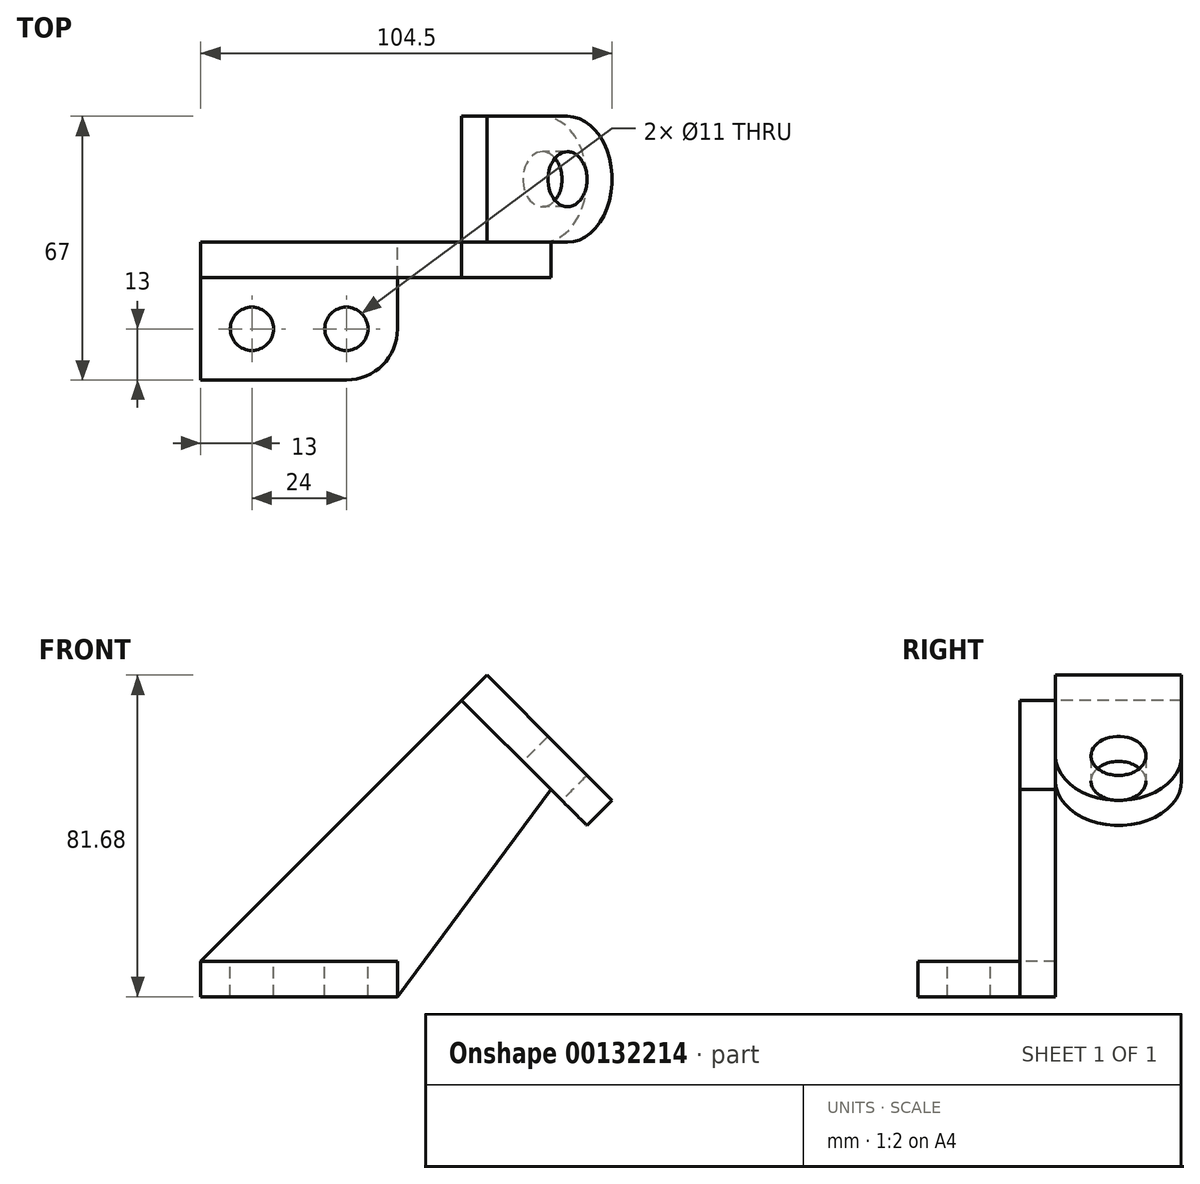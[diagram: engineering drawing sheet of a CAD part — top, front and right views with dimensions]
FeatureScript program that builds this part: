
annotation { "Feature Type Name" : "Feature", "Feature Type Description" : "" }
export const myFeature = defineFeature(function(context is Context, id is Id, definition is map)
    precondition{}
    {
        {
            var Q0;
            Q0=qCreatedBy(makeId("Front.planeOp"),FACE);
            var sketch = newSketch(context, id + "F0", { "sketchPlane" : qUnion([Q0])});
            skLineSegment(sketch, "E0", {"start": v(0, 0) * mm, "end": v(75.31, 75.31) * mm});
            skLineSegment(sketch, "E1", {"start": v(75.31, 75.31) * mm, "end": v(97.94, 52.69) * mm});
            skLineSegment(sketch, "E2", {"start": v(97.94, 52.69) * mm, "end": v(59, 0) * mm});
            skLineSegment(sketch, "E3", {"start": v(59, 0) * mm, "end": v(0, 0) * mm});
            skLineSegment(sketch, "E4", {"start": v(54.11, 66.37) * mm, "end": v(119.02, 66.37) * mm, "construction": true});
            skPoint(sketch, "E5", {"position": v(86.63, 64) * mm});
            skSolve(sketch);
        }
        {
            var Q0;
            Q0 = qSketchRegion(id + "F0", true);
            extrude(context, id + "F1", {"entities" : qUnion([Q0]), "depth" : 9 * mm});
        }
        {
            var Q0;
            Q0=makeQuery(id+"F1.opExtrude","CAP_FACE",FACE,{"disambiguationData":[OSD([sQuery(id+"F0.wireOp",EDGE,"E0"),sQuery(id+"F0.wireOp",EDGE,"E1"),sQuery(id+"F0.wireOp",EDGE,"E2"),sQuery(id+"F0.wireOp",EDGE,"E3")])],"isStart":false});
            var sketch = newSketch(context, id + "F2", { "sketchPlane" : qUnion([Q0])});
            skLineSegment(sketch, "E6.0", {"start": v(59, 0) * mm, "end": v(0, 0) * mm});
            skLineSegment(sketch, "E7", {"start": v(59, 0) * mm, "end": v(59, 9) * mm});
            skLineSegment(sketch, "E8", {"start": v(59, 9) * mm, "end": v(9, 9) * mm});
            skLineSegment(sketch, "E9.0", {"start": v(0, 0) * mm, "end": v(9, 9) * mm});
            skPoint(sketch, "E10.orphan", {"position": v(75.31, 75.31) * mm});
            skSolve(sketch);
        }
        {
            var Q0;
            Q0 = qSketchRegion(id + "F2", true);
            extrude(context, id + "F3", {"entities" : qUnion([Q0]), "operationType" : NewBodyOperationType.ADD, "depth" : 26 * mm});
        }
        {
            var Q0;
            Q0=makeQuery(id+"F3.opExtrude","CAP_FACE",FACE,{"disambiguationData":[OSD([sQuery(id+"F2.wireOp",EDGE,"E6.0"),sQuery(id+"F2.wireOp",EDGE,"E7"),sQuery(id+"F2.wireOp",EDGE,"E8"),sQuery(id+"F2.wireOp",EDGE,"E9.0")])],"isStart":false});
            var sketch = newSketch(context, id + "F4", { "sketchPlane" : qUnion([Q0])});
            skLineSegment(sketch, "E11", {"start": v(0, 0) * mm, "end": v(9, 9) * mm});
            skLineSegment(sketch, "E12", {"start": v(9, 9) * mm, "end": v(9, 0) * mm});
            skLineSegment(sketch, "E13", {"start": v(9, 0) * mm, "end": v(0, 0) * mm});
            skSolve(sketch);
        }
        {
            var Q0;
            Q0 = qSketchRegion(id + "F4", true);
            extrude(context, id + "F5", {"entities" : qUnion([Q0]), "operationType" : NewBodyOperationType.REMOVE, "endBound" : BoundingType.THROUGH_ALL, "oppositeDirection" : true, "depth" : 25 * mm});
        }
        {
            var Q0;
            Q0=makeQuery(id+"F1.opExtrude","SWEPT_FACE",FACE,{"disambiguationData":[OSD([sQuery(id+"F0.wireOp",EDGE,"E1")])]});
            var sketch = newSketch(context, id + "F6", { "sketchPlane" : qUnion([Q0])});
            skLineSegment(sketch, "E14", {"start": v(0, 0) * mm, "end": v(0, -29) * mm});
            skArc(sketch, "E15", {"start": v(0, -29) * mm, "mid": v(16, -45) * mm, "end": v(32, -29) * mm});
            skLineSegment(sketch, "E16", {"start": v(32, -29) * mm, "end": v(32, 0) * mm});
            skLineSegment(sketch, "E17", {"start": v(32, 0) * mm, "end": v(0, 0) * mm});
            skCircle(sketch, "E18", {"center": v(16, -29) * mm, "radius": 7 * mm});
            skSolve(sketch);
        }
        {
            var Q0;
            Q0 = qSketchRegion(id + "F6", true);
            extrude(context, id + "F7", {"entities" : qUnion([Q0]), "operationType" : NewBodyOperationType.ADD, "depth" : 9 * mm});
        }
        {
            var Q0;
            Q0=makeQuery(id+"F5.boolean.opBoolean","COPY",EDGE,{"derivedFrom":makeQuery(id+"F5.opExtrude","CAP_EDGE",EDGE,{"disambiguationData":[OSD([sQuery(id+"F4.wireOp",EDGE,"E12")])],"isStart":true})});
            var Q1;
            Q1=makeQuery(id+"F3.opExtrude","CAP_EDGE",EDGE,{"disambiguationData":[OSD([sQuery(id+"F2.wireOp",EDGE,"E7")])],"isStart":false});
            fillet(context, id + "F8", {"entities" : qUnion([Q0, Q1]), "radius" : 13 * mm, "tangentPropagation" : true, "allowEdgeOverflow" : false});
        }
        {
            var Q0;
            Q0=makeQuery(id+"F3.opExtrude","SWEPT_FACE",FACE,{"disambiguationData":[OSD([sQuery(id+"F2.wireOp",EDGE,"E8")])]});
            var sketch = newSketch(context, id + "F9", { "sketchPlane" : qUnion([Q0])});
            skCircle(sketch, "E19", {"center": v(22, -22) * mm, "radius": 5.5 * mm});
            skCircle(sketch, "E20", {"center": v(46, -22) * mm, "radius": 5.5 * mm});
            skSolve(sketch);
        }
        {
            var Q0;
            Q0 = qSketchRegion(id + "F9", true);
            extrude(context, id + "F10", {"entities" : qUnion([Q0]), "operationType" : NewBodyOperationType.REMOVE, "endBound" : BoundingType.THROUGH_ALL, "oppositeDirection" : true, "depth" : 25 * mm});
        }
    });
